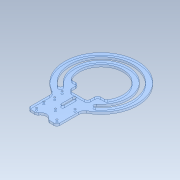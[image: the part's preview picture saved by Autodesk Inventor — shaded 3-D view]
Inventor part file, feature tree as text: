
AUTODESK INVENTOR PART (.ipt)
format: ipt  version: 2022 (Build 260153000, 153)  size: 237,056 bytes
history: native  units: mm
features: sketch x2, extrude x1
ambient origin geometry x8: Origin, YZ Plane, XZ Plane, XY Plane, X Axis, Y Axis, Z Axis, Center Point
bodies: Solid1 (feature_tree)
feature tree (3):
  sketch  "3D Sketch1"
  extrude  "Extrusion1"  [1 undecoded]
  sketch  "Sketch8"  dims[d1=3.0mm d2=0.0mm]
note: 1 required parameter value undecoded (feature->parameter linkage not recoverable at this tier; creation-order binding heuristic only, values carry confidence <= 0.55)
